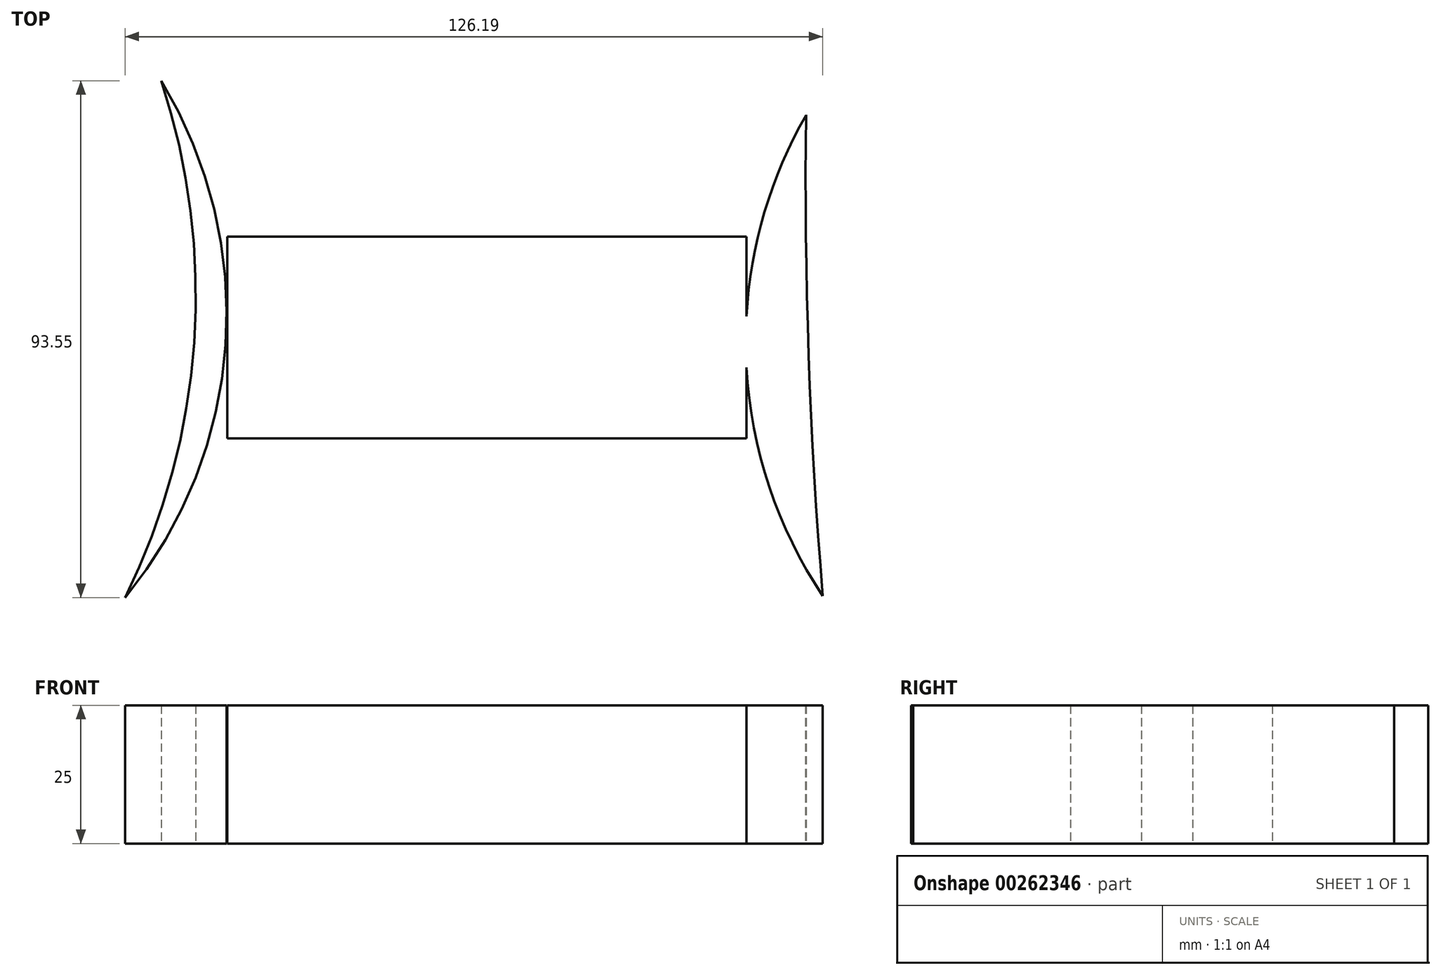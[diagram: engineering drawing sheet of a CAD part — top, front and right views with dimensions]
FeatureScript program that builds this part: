
annotation { "Feature Type Name" : "Feature", "Feature Type Description" : "" }
export const myFeature = defineFeature(function(context is Context, id is Id, definition is map)
    precondition{}
    {
        {
            var Q0;
            Q0=qCreatedBy(makeId("Top.planeOp"),FACE);
            var sketch = newSketch(context, id + "F0", { "sketchPlane" : qUnion([Q0])});
            skLineSegment(sketch, "E0.bottom", {"start": v(46.97, -18.25) * mm, "end": v(-46.97, -18.25) * mm});
            skLineSegment(sketch, "E0.top", {"start": v(46.97, 18.25) * mm, "end": v(-46.97, 18.25) * mm});
            skLineSegment(sketch, "E0.left", {"start": v(46.97, -18.25) * mm, "end": v(46.97, 18.25) * mm});
            skLineSegment(sketch, "E0.right", {"start": v(-46.97, -18.25) * mm, "end": v(-46.97, 18.25) * mm});
            skPoint(sketch, "E0.middle", {"position": v(0, 0) * mm});
            skSolve(sketch);
        }
        {
            var Q0;
            Q0=qCreatedBy(makeId("Top.planeOp"),FACE);
            var sketch = newSketch(context, id + "F1", { "sketchPlane" : qUnion([Q0])});
            skArc(sketch, "E1", {"start": v(-65.43, -47.07) * mm, "mid": v(-47.27, -1.33) * mm, "end": v(-58.91, 46.48) * mm});
            skArc(sketch, "E2", {"start": v(-65.43, -47.07) * mm, "mid": v(-52.95, -0.94) * mm, "end": v(-58.91, 46.48) * mm});
            skArc(sketch, "E3", {"start": v(57.73, 40.26) * mm, "mid": v(46.9, -3.87) * mm, "end": v(60.99, -47.07) * mm});
            skArc(sketch, "E4", {"start": v(57.73, 40.26) * mm, "mid": v(58.27, -4.63) * mm, "end": v(60.99, -49.44) * mm});
            skSolve(sketch);
        }
        {
            var Q0;
            Q0 = qSketchRegion(id + "F1", true);
            extrude(context, id + "F2", {"entities" : qUnion([Q0]), "depth" : 25 * mm});
        }
        {
            var Q0;
            Q0 = qSketchRegion(id + "F0", true);
            extrude(context, id + "F3", {"entities" : qUnion([Q0]), "operationType" : NewBodyOperationType.ADD, "depth" : 25 * mm});
        }
    });
